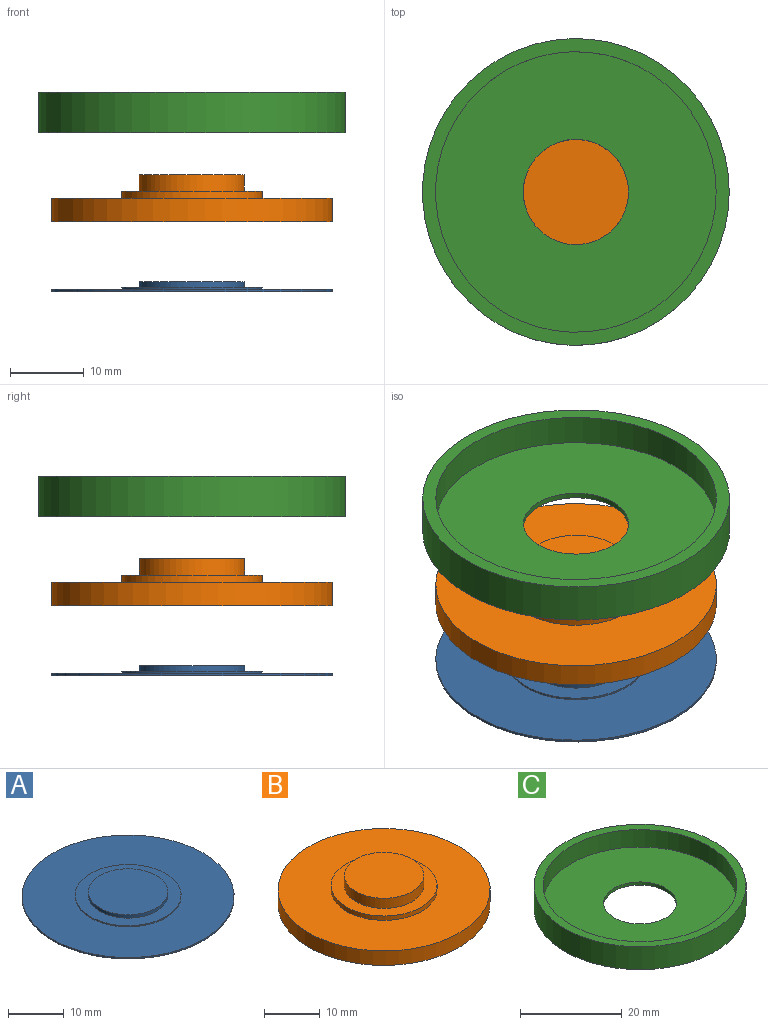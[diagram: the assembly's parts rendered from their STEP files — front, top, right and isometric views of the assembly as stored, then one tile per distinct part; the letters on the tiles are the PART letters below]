
ASSEMBLY  parts=3 mates=2
PART A: 7 faces, bbox 38.1x38.1x1.3 mm
  f0: cylinder r=19.05mm len=38.1mm, axis (0,0,-1), area 36.4mm2, adj f1,f2
  f1: plane 38.1x38.1mm, normal (0,0,1), area 855.1mm2, adj f0,f3
  f2: plane 38.1x38.1mm, normal (0,0,-1), area 1140.1mm2, adj f0
  f3: cylinder r=9.53mm len=19.05mm, axis (0,0,-1), area 15mm2, adj f1,f4
  f4: plane 19.05x19.05mm, normal (0,0,1), area 124.4mm2, adj f3,f5
  f5: cylinder r=7.15mm len=14.3mm, axis (0,0,-1), area 33.7mm2, adj f4,f6
  f6: plane 14.3x14.3mm, normal (0,0,1), area 160.6mm2, adj f5
PART B: 11 faces, bbox 38.1x38.1x6.4 mm
  f0: cylinder r=9.53mm len=19.05mm, axis (0,0,1), area 57mm2, adj f2,f6
  f1: cylinder r=19.05mm len=38.1mm, axis (0,0,1), area 380mm2, adj f2,f3
  f2: plane 38.1x38.1mm, normal (0,0,-1), area 855.1mm2, adj f0,f1
  f3: plane 38.1x38.1mm, normal (0,0,1), area 855.1mm2, adj f1,f7
  f4: plane 14.29x14.29mm, normal (0,0,-1), area 160.3mm2, adj f5
  f5: cylinder r=7.14mm len=14.29mm, axis (0,0,1), area 99.8mm2, adj f4,f6
  f6: plane 19.05x19.05mm, normal (0,0,-1), area 124.7mm2, adj f0,f5
  f7: cylinder r=9.53mm len=19.05mm, axis (0,0,-1), area 57mm2, adj f3,f8
  f8: plane 19.05x19.05mm, normal (0,0,1), area 124.7mm2, adj f7,f9
  f9: cylinder r=7.14mm len=14.29mm, axis (0,0,-1), area 99.8mm2, adj f8,f10
  f10: plane 14.29x14.29mm, normal (0,0,1), area 160.3mm2, adj f9
PART C: 10 faces, bbox 41.7x41.7x5.5 mm
  f0: plane 38.1x38.1mm, normal (0,0,1), area 979.5mm2, adj f6,f8
  f1: cylinder r=19.05mm len=38.1mm, axis (0,0,1), area 36.4mm2, adj f3,f5
  f2: cylinder r=20.83mm len=41.66mm, axis (0,0,1), area 719.1mm2, adj f3,f9
  f3: plane 41.66x41.66mm, normal (0,0,-1), area 222.7mm2, adj f1,f2
  f4: cylinder r=9.53mm len=19.05mm, axis (0,0,1), area 15mm2, adj f5,f7
  f5: plane 38.1x38.1mm, normal (0,0,-1), area 855.1mm2, adj f1,f4
  f6: cylinder r=7.15mm len=14.3mm, axis (0,0,1), area 33.7mm2, adj f0,f7
  f7: plane 19.05x19.05mm, normal (0,0,-1), area 124.4mm2, adj f4,f6
  f8: cylinder r=19.05mm len=38.1mm, axis (0,0,-1), area 501.6mm2, adj f0,f9
  f9: plane 41.66x41.66mm, normal (0,0,1), area 222.7mm2, adj f2,f8
PLACE A t=(-5.74,12.59,-20.61)mm
PLACE B t=(-5.74,12.59,-7.93)mm
PLACE C t=(-5.74,12.59,2.22)mm
MATE slider C.f1 <-> A.f0  axis (0,0,1) through (-5.74,12.59,2.22)mm
MATE slider B.f0 <-> C.f1  axis (0,0,1) through (-5.74,12.59,-4.76)mm
